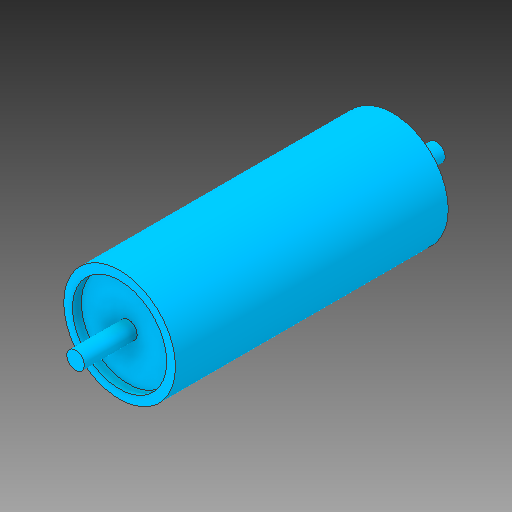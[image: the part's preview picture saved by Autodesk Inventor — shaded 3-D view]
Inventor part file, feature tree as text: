
AUTODESK INVENTOR PART (.ipt)
format: ipt  version: 2019 (Build 230136000, 136)  size: 131,584 bytes
history: native  units: mm
features: extrude x5, sketch x5
ambient origin geometry x8: Origin, YZ Plane, XZ Plane, XY Plane, X Axis, Y Axis, Z Axis, Center Point
bodies: Solid1 (feature_tree)
feature tree (10):
  extrude  "Extrusion1"  Depth=155.0mm TaperAngle=0.0deg
  extrude  "Extrusion2"  Depth=5.0mm TaperAngle=0.0deg
  extrude  "Extrusion3"  Depth=5.0mm TaperAngle=0.0deg
  extrude  "Extrusion4"  Depth=30.0mm TaperAngle=0.0deg
  extrude  "Extrusion5"  Depth=30.0mm TaperAngle=0.0deg
  sketch  "Sketch1"  dims[d0=31.75mm d1=155.0mm d2=0.0mm]
  sketch  "Sketch2"  dims[d3=26.75mm d4=5.0mm d5=0.0mm]
  sketch  "Sketch3"  dims[d6=26.75mm d7=5.0mm d8=0.0mm]
  sketch  "Sketch4"  dims[d9=5.0mm d10=30.0mm d11=0.0mm]
  sketch  "Sketch5"  dims[d12=5.0mm d13=30.0mm d14=0.0mm]
